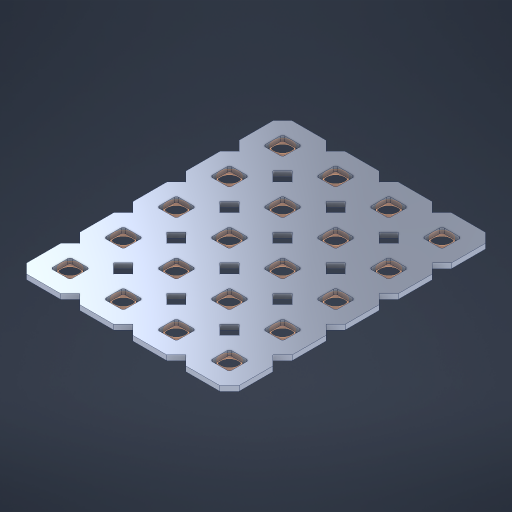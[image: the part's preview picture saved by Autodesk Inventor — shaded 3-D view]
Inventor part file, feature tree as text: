
AUTODESK INVENTOR PART (.ipt)
format: ipt  version: 2023 (Build 270158000, 158)  size: 489,984 bytes
history: native  units: in
note: dims shown in document units (in); Inventor stores cm internally (conversion verified against a paired STEP export)
features: other x21, extrude x19, sketch x2, pattern_linear x1
ambient origin geometry x8: Origin, YZ Plane, XZ Plane, XY Plane, X Axis, Y Axis, Z Axis, Center Point
bodies: Solid1 (feature_tree), Body (feature_tree)
feature tree (43):
  pattern_linear  "Rectangular Pattern1"  Spacing1=0.09in  [1 undecoded]
  sketch  "Sketch1"  dims[d1=0.5in]
  sketch  "Sketch2"  dims[d2=0.182in d3=0.09in d4=0.09in d5=0.09in d6=0.09in d7=0.09in d8=0.09in d9=0.09in d10=0.09in d11=0.02in d13=0.0in d14=0.172in d15=0.0625in d16=0.0in d19=0.5in d22=0.5in]
  other  "Srf1"
  other  "Srf126"
  other  "Srf127"
  other  "Srf128"
  other  "Srf129"
  other  "Srf268"
  other  "Srf269"
  other  "Srf270"
  other  "Srf271"
  other  "Srf272"
  other  "Srf293"
  other  "Srf294"
  other  "Srf295"
  other  "Srf296"
  other  "Srf297"
  other  "Srf318"
  other  "Srf319"
  other  "Srf320"
  other  "Srf321"
  other  "Srf322"
  other  "Circle"
  extrude  "ExtrusionSrf126"  Depth=0.09in
  extrude  "ExtrusionSrf127"  Depth=0.09in
  extrude  "ExtrusionSrf128"  Depth=0.09in
  extrude  "ExtrusionSrf129"  Depth=0.09in
  extrude  "ExtrusionSrf268"  Depth=0.09in
  extrude  "ExtrusionSrf269"  Depth=0.09in
  extrude  "ExtrusionSrf270"  Depth=0.09in
  extrude  "ExtrusionSrf271"  Depth=0.02in
  extrude  "ExtrusionSrf272"  TaperAngle=0.0deg  [1 undecoded]
  extrude  "ExtrusionSrf293"  Depth=0.5in
  extrude  "ExtrusionSrf294"  Depth=0.5in TaperAngle=0.0deg
  extrude  "ExtrusionSrf295"  Depth=0.5in
  extrude  "ExtrusionSrf296"  Depth=0.5in
  extrude  "ExtrusionSrf297"  [1 undecoded]
  extrude  "ExtrusionSrf318"  [1 undecoded]
  extrude  "ExtrusionSrf319"  [1 undecoded]
  extrude  "ExtrusionSrf320"  [1 undecoded]
  extrude  "ExtrusionSrf321"  [1 undecoded]
  extrude  "ExtrusionSrf322"  [1 undecoded]
note: 8 required parameter values undecoded (feature->parameter linkage not recoverable at this tier; creation-order binding heuristic only, values carry confidence <= 0.55)
